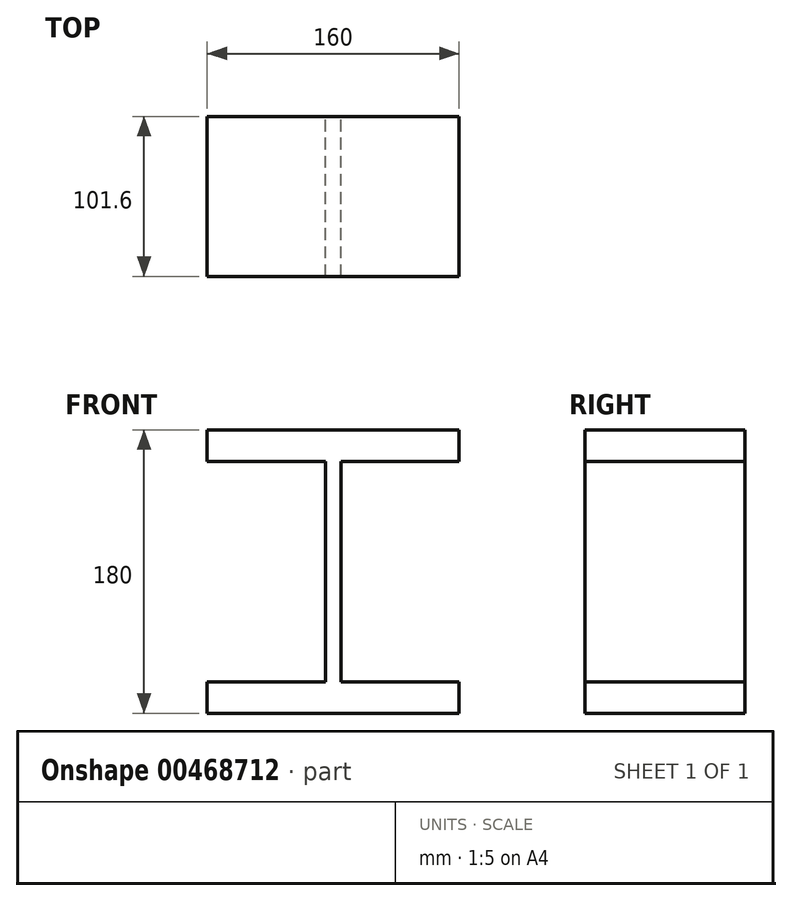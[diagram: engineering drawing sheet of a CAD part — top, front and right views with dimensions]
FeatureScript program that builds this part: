
annotation { "Feature Type Name" : "Feature", "Feature Type Description" : "" }
export const myFeature = defineFeature(function(context is Context, id is Id, definition is map)
    precondition{}
    {
        {
            var Q0;
            Q0=qCreatedBy(makeId("Front.planeOp"),FACE);
            var sketch = newSketch(context, id + "F0", { "sketchPlane" : qUnion([Q0])});
            skLineSegment(sketch, "E0", {"start": v(-80, 90) * mm, "end": v(80, 90) * mm});
            skLineSegment(sketch, "E1", {"start": v(80, 90) * mm, "end": v(80, 70) * mm});
            skLineSegment(sketch, "E2", {"start": v(80, 70) * mm, "end": v(5, 70) * mm});
            skLineSegment(sketch, "E3", {"start": v(5, 70) * mm, "end": v(5, 0) * mm});
            skLineSegment(sketch, "E4.MirrorCS", {"start": v(-5, 70) * mm, "end": v(-5, 0) * mm});
            skLineSegment(sketch, "E5.MirrorCS", {"start": v(-80, 90) * mm, "end": v(-80, 70) * mm});
            skLineSegment(sketch, "E6.MirrorCS", {"start": v(-80, 70) * mm, "end": v(-5, 70) * mm});
            skLineSegment(sketch, "E7.MirrorCS", {"start": v(-5, -70) * mm, "end": v(-5, 0) * mm});
            skLineSegment(sketch, "E8.MirrorCS", {"start": v(5, -70) * mm, "end": v(5, 0) * mm});
            skLineSegment(sketch, "E9.MirrorCS", {"start": v(-80, -90) * mm, "end": v(80, -90) * mm});
            skLineSegment(sketch, "E10.MirrorCS", {"start": v(-80, -70) * mm, "end": v(-5, -70) * mm});
            skLineSegment(sketch, "E11.MirrorCS", {"start": v(80, -70) * mm, "end": v(5, -70) * mm});
            skLineSegment(sketch, "E12.MirrorCS", {"start": v(-80, -90) * mm, "end": v(-80, -70) * mm});
            skLineSegment(sketch, "E13.MirrorCS", {"start": v(80, -90) * mm, "end": v(80, -70) * mm});
            skSolve(sketch);
        }
        {
            var Q0;
            Q0=makeQuery(id+"F0.imprint","IMPRINT",FACE,{"disambiguationData":[TD([[makeQuery(id+"F0.imprint","IMPRINT",EDGE,{"derivedFrom":sQuery(id+"F0.wireOp",EDGE,"E0")}),-1.0]])]});
            extrude(context, id + "F1", {"entities" : qUnion([Q0]), "depth" : 101.6 * mm});
        }
    });
